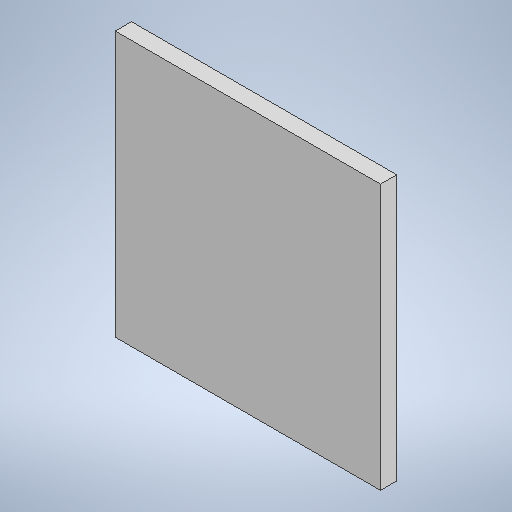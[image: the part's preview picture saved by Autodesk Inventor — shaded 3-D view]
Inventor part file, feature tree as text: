
AUTODESK INVENTOR PART (.ipt)
format: ipt  version: 2025.1 (Build 291241020, 241B)  size: 201,728 bytes
history: native  units: in
note: dims shown in document units (in); Inventor stores cm internally (conversion verified against a paired STEP export)
features: extrude x1, sketch x1
ambient origin geometry x8: Origin, YZ Plane, XZ Plane, XY Plane, X Axis, Y Axis, Z Axis, Center Point
bodies: Solid1 (feature_tree)
feature tree (2):
  extrude  "Extrusion1"  [1 undecoded]
  sketch  "Sketch1"  dims[d27=0.367in d28=0.0in]
note: 1 required parameter value undecoded (feature->parameter linkage not recoverable at this tier; creation-order binding heuristic only, values carry confidence <= 0.55)
